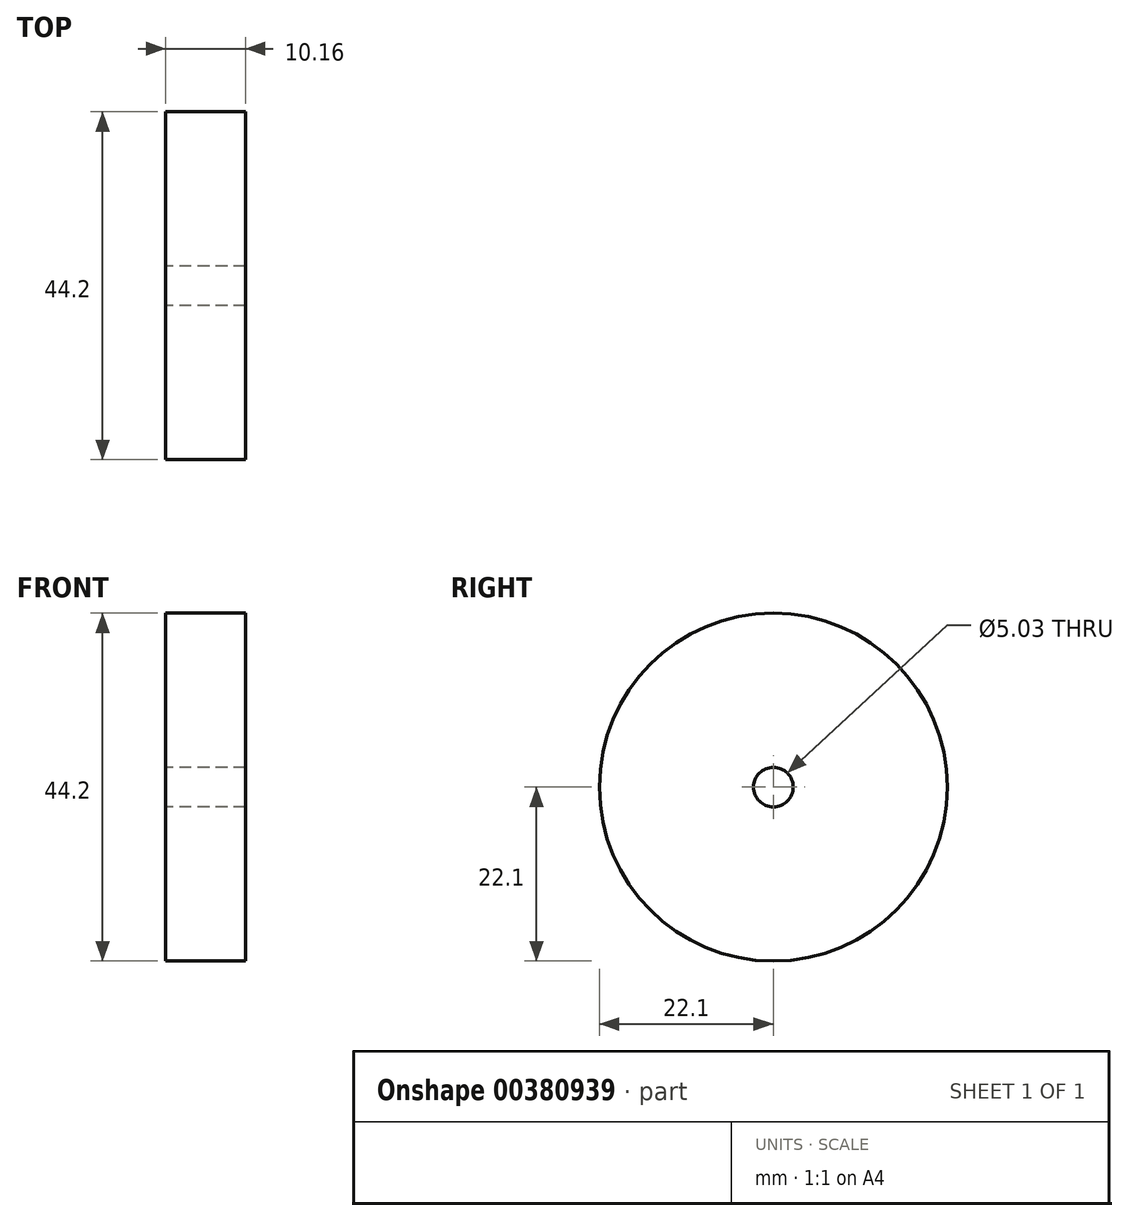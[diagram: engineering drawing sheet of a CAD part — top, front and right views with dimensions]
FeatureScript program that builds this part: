
annotation { "Feature Type Name" : "Feature", "Feature Type Description" : "" }
export const myFeature = defineFeature(function(context is Context, id is Id, definition is map)
    precondition{}
    {
        {
            var Q0;
            Q0=qCreatedBy(makeId("Right.planeOp"),FACE);
            var sketch = newSketch(context, id + "F0", { "sketchPlane" : qUnion([Q0])});
            skCircle(sketch, "E0", {"center": v(0, 0) * mm, "radius": 22.1 * mm});
            skCircle(sketch, "E1", {"center": v(0, 0) * mm, "radius": 2.52 * mm});
            skSolve(sketch);
        }
        {
            var Q0;
            Q0=makeQuery(id+"F0.imprint","IMPRINT",FACE,{"disambiguationData":[TD([[makeQuery(id+"F0.imprint","IMPRINT",EDGE,{"derivedFrom":sQuery(id+"F0.wireOp",EDGE,"E0")}),1.0]])]});
            extrude(context, id + "F1", {"entities" : qUnion([Q0]), "depth" : 10.16 * mm});
        }
    });
